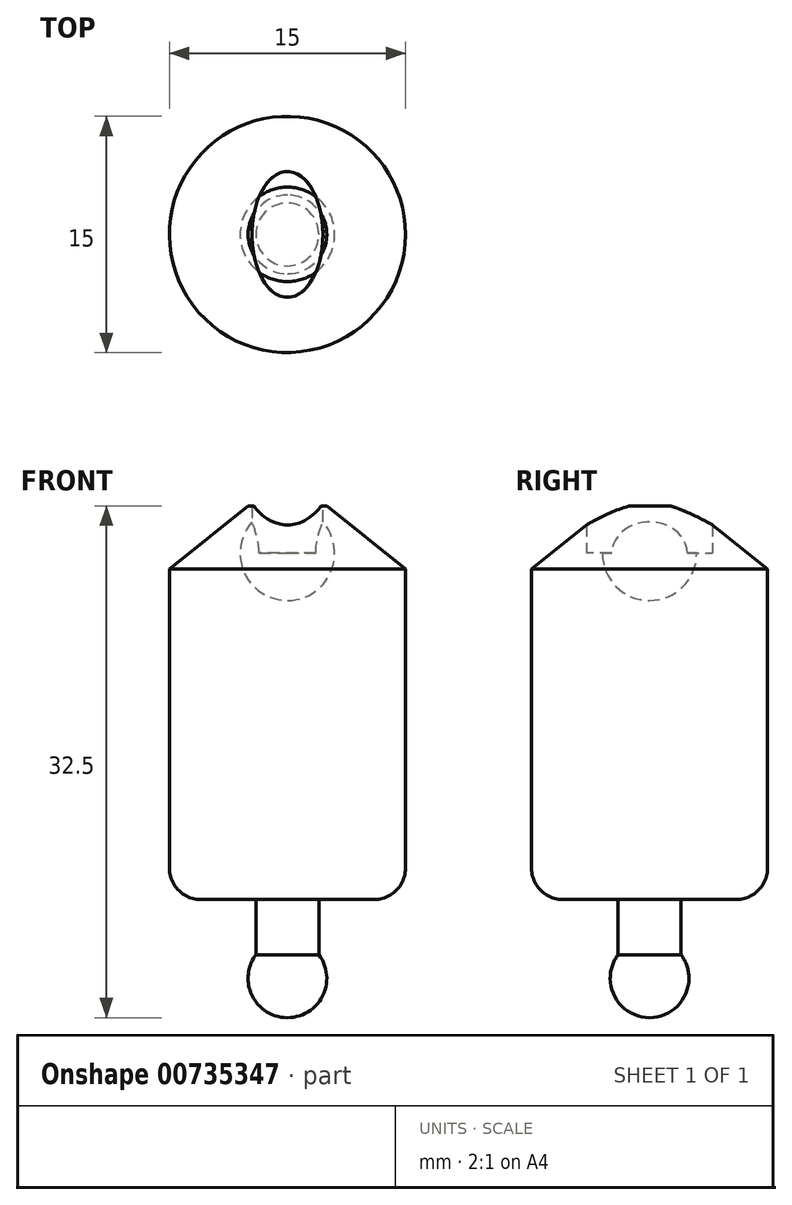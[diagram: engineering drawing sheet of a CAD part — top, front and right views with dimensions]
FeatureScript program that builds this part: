
annotation { "Feature Type Name" : "Feature", "Feature Type Description" : "" }
export const myFeature = defineFeature(function(context is Context, id is Id, definition is map)
    precondition{}
    {
        {
            var Q0;
            Q0=qCreatedBy(makeId("Top.planeOp"),FACE);
            var sketch = newSketch(context, id + "F0", { "sketchPlane" : qUnion([Q0])});
            skCircle(sketch, "E0", {"center": v(0, 0) * mm, "radius": 7.5 * mm});
            skSolve(sketch);
        }
        {
            var Q0;
            Q0 = qSketchRegion(id + "F0", true);
            extrude(context, id + "F1", {"entities" : qUnion([Q0]), "depth" : 25 * mm, "offsetDistance" : 25 * mm});
        }
        {
            var Q0;
            Q0=makeQuery(id+"F1.opExtrude","CAP_FACE",FACE,{"disambiguationData":[OSD([sQuery(id+"F0.wireOp",EDGE,"E0")])],"isStart":true});
            var sketch = newSketch(context, id + "F2", { "sketchPlane" : qUnion([Q0])});
            skCircle(sketch, "E1", {"center": v(0, 0) * mm, "radius": 2 * mm});
            skSolve(sketch);
        }
        {
            var Q0;
            Q0 = qSketchRegion(id + "F2", true);
            extrude(context, id + "F3", {"entities" : qUnion([Q0]), "operationType" : NewBodyOperationType.ADD, "depth" : 5 * mm, "offsetDistance" : 25 * mm});
        }
        {
            var Q0;
            Q0=makeQuery(id+"F3.opExtrude","CAP_FACE",FACE,{"disambiguationData":[OSD([sQuery(id+"F2.wireOp",EDGE,"E1")])],"isStart":false});
            var sketch = newSketch(context, id + "F4", { "sketchPlane" : qUnion([Q0])});
            skCircle(sketch, "E2", {"center": v(0, 0) * mm, "radius": 2.5 * mm});
            skLineSegment(sketch, "E3", {"start": v(0, 2.5) * mm, "end": v(0, -2.5) * mm});
            skSolve(sketch);
        }
        {
            var Q0;
            {var subQ0=sQuery(id+"F4.wireOp",EDGE,"E3");var subQ1=sQuery(id+"F4.wireOp",EDGE,"E2");var subQ2=makeQuery(id+"F4.imprint","INTERSECT",VERTEX,{"disambiguationData":[OD(0.0)],"derivedFrom":[subQ1,subQ0]});Q0=makeQuery(id+"F4.imprint","IMPRINT",FACE,{"disambiguationData":[TD([[makeQuery(id+"F4.imprint","IMPRINT",EDGE,{"disambiguationData":[TD([[subQ2,-1.0]])],"derivedFrom":subQ1}),1.0]])]});}
            var Q1;
            {var subQ0=sQuery(id+"F4.wireOp",EDGE,"E3");var subQ1=makeQuery(id+"F3.opExtrude","CAP_EDGE",EDGE,{"disambiguationData":[OSD([sQuery(id+"F2.wireOp",EDGE,"E1")])],"isStart":false});var subQ2=makeQuery(id+"F4.imprint","INTERSECT",VERTEX,{"disambiguationData":[OD(0.0)],"derivedFrom":[subQ1,subQ0]});Q1=makeQuery(id+"F4.imprint","IMPRINT",FACE,{"disambiguationData":[TD([[makeQuery(id+"F4.imprint","IMPRINT",EDGE,{"disambiguationData":[TD([[subQ2,-1.0]])],"derivedFrom":subQ0}),-1.0]])]});}
            var Q2;
            Q2=sQuery(id+"F4.wireOp",EDGE,"E3");
            revolve(context, id + "F5", {"operationType" : NewBodyOperationType.ADD, "surfaceOperationType" : NewSurfaceOperationType.NEW, "entities" : qUnion([Q0, Q1]), "axis" : qUnion([Q2]), "revolveType" : RevolveType.FULL});
        }
        {
            var Q0;
            Q0=makeQuery(id+"F1.opExtrude","CAP_FACE",FACE,{"disambiguationData":[OSD([sQuery(id+"F0.wireOp",EDGE,"E0")])],"isStart":false});
            var sketch = newSketch(context, id + "F6", { "sketchPlane" : qUnion([Q0])});
            skEllipse(sketch, "E4", {"center": v(0, 0) * mm, "majorRadius": 4 * mm, "minorRadius": 2.25 * mm, "majorAxis": v(0, 1)});
            skSolve(sketch);
        }
        {
            var Q0;
            Q0 = qSketchRegion(id + "F6", true);
            extrude(context, id + "F7", {"entities" : qUnion([Q0]), "operationType" : NewBodyOperationType.REMOVE, "oppositeDirection" : true, "depth" : 3 * mm, "offsetDistance" : 25 * mm});
        }
        {
            var Q0;
            Q0=makeQuery(id+"F7.boolean.opBoolean","COPY",FACE,{"derivedFrom":makeQuery(id+"F7.opExtrude","CAP_FACE",FACE,{"disambiguationData":[OSD([sQuery(id+"F6.wireOp",EDGE,"E4")])],"isStart":false})});
            var sketch = newSketch(context, id + "F8", { "sketchPlane" : qUnion([Q0])});
            skCircle(sketch, "E5", {"center": v(0, 0) * mm, "radius": 3 * mm});
            skLineSegment(sketch, "E6", {"start": v(0, 3) * mm, "end": v(0, -3) * mm});
            skSolve(sketch);
        }
        {
            var Q0;
            {var subQ0=sQuery(id+"F8.wireOp",EDGE,"E5");var subQ1=makeQuery(id+"F7.boolean.opBoolean","COPY",EDGE,{"derivedFrom":makeQuery(id+"F7.opExtrude","CAP_EDGE",EDGE,{"disambiguationData":[OSD([sQuery(id+"F6.wireOp",EDGE,"E4")])],"isStart":false})});var subQ2=makeQuery(id+"F8.imprint","INTERSECT",VERTEX,{"disambiguationData":[OD(1.0)],"derivedFrom":[subQ1,subQ0]});Q0=makeQuery(id+"F8.imprint","IMPRINT",FACE,{"disambiguationData":[TD([[makeQuery(id+"F8.imprint","IMPRINT",EDGE,{"disambiguationData":[TD([[subQ2,-1.0]])],"derivedFrom":subQ0}),1.0]])]});}
            var Q1;
            {var subQ0=sQuery(id+"F8.wireOp",EDGE,"E5");var subQ1=makeQuery(id+"F7.boolean.opBoolean","COPY",EDGE,{"derivedFrom":makeQuery(id+"F7.opExtrude","CAP_EDGE",EDGE,{"disambiguationData":[OSD([sQuery(id+"F6.wireOp",EDGE,"E4")])],"isStart":false})});var subQ2=makeQuery(id+"F8.imprint","INTERSECT",VERTEX,{"disambiguationData":[OD(0.0)],"derivedFrom":[subQ1,subQ0]});Q1=makeQuery(id+"F8.imprint","IMPRINT",FACE,{"disambiguationData":[TD([[makeQuery(id+"F8.imprint","IMPRINT",EDGE,{"disambiguationData":[TD([[subQ2,1.0]])],"derivedFrom":subQ0}),1.0]])]});}
            var Q2;
            {var subQ0=sQuery(id+"F8.wireOp",EDGE,"E6");Q2=makeQuery(id+"F8.imprint","IMPRINT",FACE,{"disambiguationData":[TD([[makeQuery(id+"F8.imprint","IMPRINT",EDGE,{"derivedFrom":subQ0}),-1.0]])]});}
            var Q3;
            Q3=sQuery(id+"F8.wireOp",EDGE,"E6");
            revolve(context, id + "F9", {"operationType" : NewBodyOperationType.REMOVE, "surfaceOperationType" : NewSurfaceOperationType.NEW, "entities" : qUnion([Q0, Q1, Q2]), "axis" : qUnion([Q3]), "revolveType" : RevolveType.FULL, "oppositeDirection" : true});
        }
        {
            var Q0;
            Q0=makeQuery(id+"F1.opExtrude","CAP_EDGE",EDGE,{"disambiguationData":[OSD([sQuery(id+"F0.wireOp",EDGE,"E0")])],"isStart":false});
            chamfer(context, id + "F10", {"entities" : qUnion([Q0]), "chamferType" : ChamferType.TWO_OFFSETS, "width1" : 5 * mm, "oppositeDirection" : false, "width2" : 4 * mm, "tangentPropagation" : true});
        }
        {
            var Q0;
            Q0=makeQuery(id+"F1.opExtrude","CAP_EDGE",EDGE,{"disambiguationData":[OSD([sQuery(id+"F0.wireOp",EDGE,"E0")])],"isStart":true});
            fillet(context, id + "F11", {"entities" : qUnion([Q0]), "radius" : 2 * mm, "tangentPropagation" : true, "allowEdgeOverflow" : false});
        }
    });
